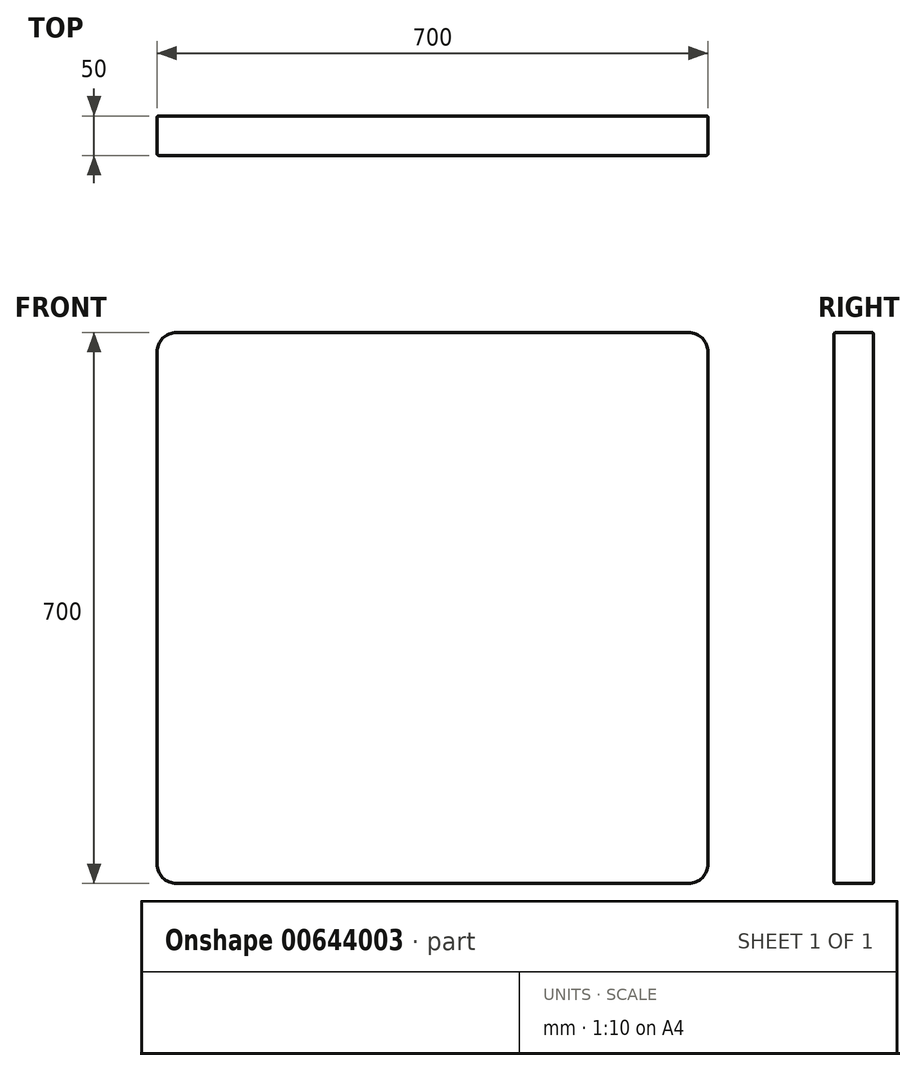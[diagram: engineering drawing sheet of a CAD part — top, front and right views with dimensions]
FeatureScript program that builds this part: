
annotation { "Feature Type Name" : "Feature", "Feature Type Description" : "" }
export const myFeature = defineFeature(function(context is Context, id is Id, definition is map)
    precondition{}
    {
        {
            var Q0;
            Q0=qCreatedBy(makeId("Front.planeOp"),FACE);
            var sketch = newSketch(context, id + "F0", { "sketchPlane" : qUnion([Q0])});
            skLineSegment(sketch, "E0.bottom", {"start": v(350, 350) * mm, "end": v(-350, 350) * mm});
            skLineSegment(sketch, "E0.top", {"start": v(350, -350) * mm, "end": v(-350, -350) * mm});
            skLineSegment(sketch, "E0.left", {"start": v(350, 350) * mm, "end": v(350, -350) * mm});
            skLineSegment(sketch, "E0.right", {"start": v(-350, 350) * mm, "end": v(-350, -350) * mm});
            skPoint(sketch, "E0.middle", {"position": v(0, 0) * mm});
            skSolve(sketch);
        }
        {
            var Q0;
            Q0=qSketchRegion(id+"F0",true);
            extrude(context, id + "F1", {"entities" : qUnion([Q0]), "depth" : 50 * mm, "offsetDistance" : 25 * mm});
        }
        {
            var Q0;
            Q0=makeQuery(id+"F1.opExtrude","SWEPT_EDGE",EDGE,{"disambiguationData":[OSD([sQuery(id+"F0.wireOp",EDGE,"E0.bottom"),sQuery(id+"F0.wireOp",EDGE,"E0.right")])]});
            var Q1;
            Q1=makeQuery(id+"F1.opExtrude","SWEPT_EDGE",EDGE,{"disambiguationData":[OSD([sQuery(id+"F0.wireOp",EDGE,"E0.top"),sQuery(id+"F0.wireOp",EDGE,"E0.right")])]});
            var Q2;
            Q2=makeQuery(id+"F1.opExtrude","SWEPT_EDGE",EDGE,{"disambiguationData":[OSD([sQuery(id+"F0.wireOp",EDGE,"E0.top"),sQuery(id+"F0.wireOp",EDGE,"E0.left")])]});
            var Q3;
            Q3=makeQuery(id+"F1.opExtrude","SWEPT_EDGE",EDGE,{"disambiguationData":[OSD([sQuery(id+"F0.wireOp",EDGE,"E0.bottom"),sQuery(id+"F0.wireOp",EDGE,"E0.left")])]});
            fillet(context, id + "F2", {"entities" : qUnion([Q0, Q1, Q2, Q3]), "radius" : 25 * mm, "tangentPropagation" : true, "allowEdgeOverflow" : false});
        }
        {
            var Q0;
            Q0=makeQuery(id+"F1.opExtrude","CAP_EDGE",EDGE,{"disambiguationData":[OSD([sQuery(id+"F0.wireOp",EDGE,"E0.left")])],"isStart":false});
            var Q1;
            Q1=makeQuery(id+"F1.opExtrude","CAP_EDGE",EDGE,{"disambiguationData":[OSD([sQuery(id+"F0.wireOp",EDGE,"E0.bottom")])],"isStart":false});
            var Q2;
            Q2=makeQuery(id+"F1.opExtrude","CAP_EDGE",EDGE,{"disambiguationData":[OSD([sQuery(id+"F0.wireOp",EDGE,"E0.right")])],"isStart":false});
            var Q3;
            {var subQ0=sQuery(id+"F0.wireOp",EDGE,"E0.right");var subQ1=sQuery(id+"F0.wireOp",EDGE,"E0.bottom");Q3=makeQuery(id+"F2.opFillet","BLEND_EDGE",EDGE,{"blendedFrom":[makeQuery(id+"F1.opExtrude","SWEPT_EDGE",EDGE,{"disambiguationData":[OSD([subQ1,subQ0])]}),makeQuery(id+"F1.opExtrude","CAP_FACE",FACE,{"disambiguationData":[OSD([subQ1,sQuery(id+"F0.wireOp",EDGE,"E0.top"),sQuery(id+"F0.wireOp",EDGE,"E0.left"),subQ0])],"isStart":false})],"blendedInto":[makeQuery(id+"F1.opExtrude","CAP_FACE",FACE,{"disambiguationData":[OSD([subQ1,sQuery(id+"F0.wireOp",EDGE,"E0.top"),sQuery(id+"F0.wireOp",EDGE,"E0.left"),subQ0])],"isStart":false})]});}
            var Q4;
            {var subQ0=sQuery(id+"F0.wireOp",EDGE,"E0.right");var subQ1=sQuery(id+"F0.wireOp",EDGE,"E0.top");Q4=makeQuery(id+"F2.opFillet","BLEND_EDGE",EDGE,{"blendedFrom":[makeQuery(id+"F1.opExtrude","SWEPT_EDGE",EDGE,{"disambiguationData":[OSD([subQ1,subQ0])]}),makeQuery(id+"F1.opExtrude","CAP_FACE",FACE,{"disambiguationData":[OSD([sQuery(id+"F0.wireOp",EDGE,"E0.bottom"),subQ1,sQuery(id+"F0.wireOp",EDGE,"E0.left"),subQ0])],"isStart":false})],"blendedInto":[makeQuery(id+"F1.opExtrude","CAP_FACE",FACE,{"disambiguationData":[OSD([sQuery(id+"F0.wireOp",EDGE,"E0.bottom"),subQ1,sQuery(id+"F0.wireOp",EDGE,"E0.left"),subQ0])],"isStart":false})]});}
            var Q5;
            Q5=makeQuery(id+"F1.opExtrude","CAP_EDGE",EDGE,{"disambiguationData":[OSD([sQuery(id+"F0.wireOp",EDGE,"E0.top")])],"isStart":false});
            var Q6;
            {var subQ0=sQuery(id+"F0.wireOp",EDGE,"E0.left");var subQ1=sQuery(id+"F0.wireOp",EDGE,"E0.top");Q6=makeQuery(id+"F2.opFillet","BLEND_EDGE",EDGE,{"blendedFrom":[makeQuery(id+"F1.opExtrude","SWEPT_EDGE",EDGE,{"disambiguationData":[OSD([subQ1,subQ0])]}),makeQuery(id+"F1.opExtrude","CAP_FACE",FACE,{"disambiguationData":[OSD([sQuery(id+"F0.wireOp",EDGE,"E0.bottom"),subQ1,subQ0,sQuery(id+"F0.wireOp",EDGE,"E0.right")])],"isStart":false})],"blendedInto":[makeQuery(id+"F1.opExtrude","CAP_FACE",FACE,{"disambiguationData":[OSD([sQuery(id+"F0.wireOp",EDGE,"E0.bottom"),subQ1,subQ0,sQuery(id+"F0.wireOp",EDGE,"E0.right")])],"isStart":false})]});}
            var Q7;
            {var subQ0=sQuery(id+"F0.wireOp",EDGE,"E0.left");var subQ1=sQuery(id+"F0.wireOp",EDGE,"E0.bottom");Q7=makeQuery(id+"F2.opFillet","BLEND_EDGE",EDGE,{"blendedFrom":[makeQuery(id+"F1.opExtrude","SWEPT_EDGE",EDGE,{"disambiguationData":[OSD([subQ1,subQ0])]}),makeQuery(id+"F1.opExtrude","CAP_FACE",FACE,{"disambiguationData":[OSD([subQ1,sQuery(id+"F0.wireOp",EDGE,"E0.top"),subQ0,sQuery(id+"F0.wireOp",EDGE,"E0.right")])],"isStart":false})],"blendedInto":[makeQuery(id+"F1.opExtrude","CAP_FACE",FACE,{"disambiguationData":[OSD([subQ1,sQuery(id+"F0.wireOp",EDGE,"E0.top"),subQ0,sQuery(id+"F0.wireOp",EDGE,"E0.right")])],"isStart":false})]});}
            var Q8;
            Q8=makeQuery(id+"F1.opExtrude","CAP_EDGE",EDGE,{"disambiguationData":[OSD([sQuery(id+"F0.wireOp",EDGE,"E0.bottom")])],"isStart":true});
            var Q9;
            {var subQ0=sQuery(id+"F0.wireOp",EDGE,"E0.left");var subQ1=sQuery(id+"F0.wireOp",EDGE,"E0.bottom");Q9=makeQuery(id+"F2.opFillet","BLEND_EDGE",EDGE,{"blendedFrom":[makeQuery(id+"F1.opExtrude","SWEPT_EDGE",EDGE,{"disambiguationData":[OSD([subQ1,subQ0])]}),makeQuery(id+"F1.opExtrude","CAP_FACE",FACE,{"disambiguationData":[OSD([subQ1,sQuery(id+"F0.wireOp",EDGE,"E0.top"),subQ0,sQuery(id+"F0.wireOp",EDGE,"E0.right")])],"isStart":true})],"blendedInto":[makeQuery(id+"F1.opExtrude","CAP_FACE",FACE,{"disambiguationData":[OSD([subQ1,sQuery(id+"F0.wireOp",EDGE,"E0.top"),subQ0,sQuery(id+"F0.wireOp",EDGE,"E0.right")])],"isStart":true})]});}
            var Q10;
            Q10=makeQuery(id+"F1.opExtrude","CAP_EDGE",EDGE,{"disambiguationData":[OSD([sQuery(id+"F0.wireOp",EDGE,"E0.left")])],"isStart":true});
            var Q11;
            {var subQ0=sQuery(id+"F0.wireOp",EDGE,"E0.left");var subQ1=sQuery(id+"F0.wireOp",EDGE,"E0.top");Q11=makeQuery(id+"F2.opFillet","BLEND_EDGE",EDGE,{"blendedFrom":[makeQuery(id+"F1.opExtrude","SWEPT_EDGE",EDGE,{"disambiguationData":[OSD([subQ1,subQ0])]}),makeQuery(id+"F1.opExtrude","CAP_FACE",FACE,{"disambiguationData":[OSD([sQuery(id+"F0.wireOp",EDGE,"E0.bottom"),subQ1,subQ0,sQuery(id+"F0.wireOp",EDGE,"E0.right")])],"isStart":true})],"blendedInto":[makeQuery(id+"F1.opExtrude","CAP_FACE",FACE,{"disambiguationData":[OSD([sQuery(id+"F0.wireOp",EDGE,"E0.bottom"),subQ1,subQ0,sQuery(id+"F0.wireOp",EDGE,"E0.right")])],"isStart":true})]});}
            var Q12;
            Q12=makeQuery(id+"F1.opExtrude","CAP_EDGE",EDGE,{"disambiguationData":[OSD([sQuery(id+"F0.wireOp",EDGE,"E0.top")])],"isStart":true});
            var Q13;
            {var subQ0=sQuery(id+"F0.wireOp",EDGE,"E0.right");var subQ1=sQuery(id+"F0.wireOp",EDGE,"E0.top");Q13=makeQuery(id+"F2.opFillet","BLEND_EDGE",EDGE,{"blendedFrom":[makeQuery(id+"F1.opExtrude","SWEPT_EDGE",EDGE,{"disambiguationData":[OSD([subQ1,subQ0])]}),makeQuery(id+"F1.opExtrude","CAP_FACE",FACE,{"disambiguationData":[OSD([sQuery(id+"F0.wireOp",EDGE,"E0.bottom"),subQ1,sQuery(id+"F0.wireOp",EDGE,"E0.left"),subQ0])],"isStart":true})],"blendedInto":[makeQuery(id+"F1.opExtrude","CAP_FACE",FACE,{"disambiguationData":[OSD([sQuery(id+"F0.wireOp",EDGE,"E0.bottom"),subQ1,sQuery(id+"F0.wireOp",EDGE,"E0.left"),subQ0])],"isStart":true})]});}
            var Q14;
            Q14=makeQuery(id+"F1.opExtrude","CAP_EDGE",EDGE,{"disambiguationData":[OSD([sQuery(id+"F0.wireOp",EDGE,"E0.right")])],"isStart":true});
            var Q15;
            {var subQ0=sQuery(id+"F0.wireOp",EDGE,"E0.right");var subQ1=sQuery(id+"F0.wireOp",EDGE,"E0.bottom");Q15=makeQuery(id+"F2.opFillet","BLEND_EDGE",EDGE,{"blendedFrom":[makeQuery(id+"F1.opExtrude","SWEPT_EDGE",EDGE,{"disambiguationData":[OSD([subQ1,subQ0])]}),makeQuery(id+"F1.opExtrude","CAP_FACE",FACE,{"disambiguationData":[OSD([subQ1,sQuery(id+"F0.wireOp",EDGE,"E0.top"),sQuery(id+"F0.wireOp",EDGE,"E0.left"),subQ0])],"isStart":true})],"blendedInto":[makeQuery(id+"F1.opExtrude","CAP_FACE",FACE,{"disambiguationData":[OSD([subQ1,sQuery(id+"F0.wireOp",EDGE,"E0.top"),sQuery(id+"F0.wireOp",EDGE,"E0.left"),subQ0])],"isStart":true})]});}
            fillet(context, id + "F3", {"entities" : qUnion([Q0, Q1, Q2, Q3, Q4, Q5, Q6, Q7, Q8, Q9, Q10, Q11, Q12, Q13, Q14, Q15]), "radius" : 2 * mm, "tangentPropagation" : true, "allowEdgeOverflow" : false});
        }
    });
